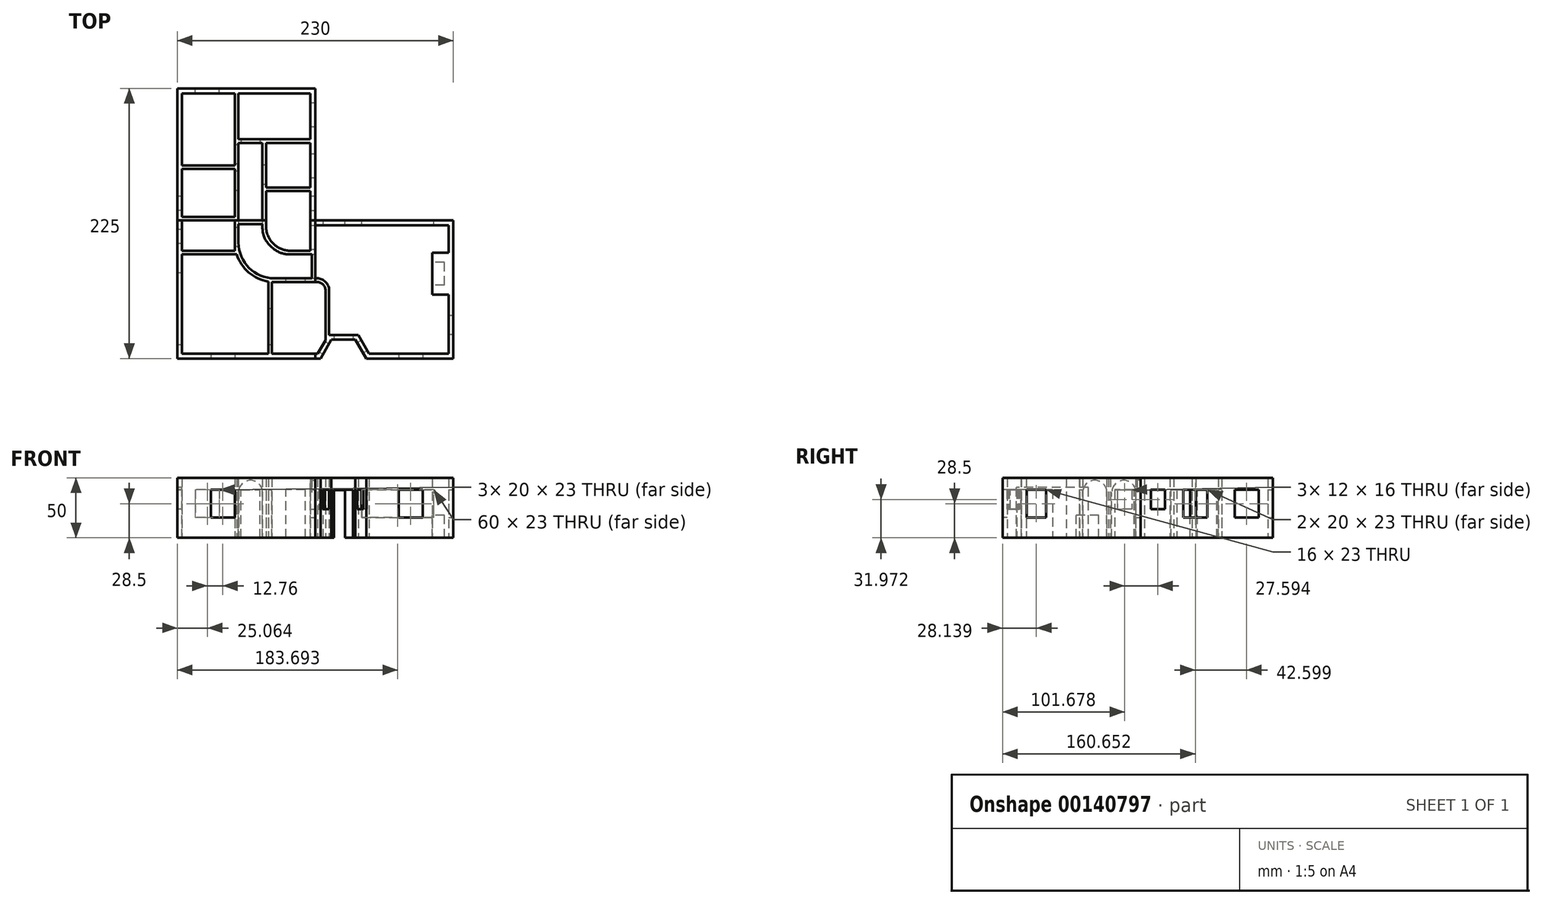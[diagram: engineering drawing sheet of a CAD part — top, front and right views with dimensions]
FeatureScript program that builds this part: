
annotation { "Feature Type Name" : "Feature", "Feature Type Description" : "" }
export const myFeature = defineFeature(function(context is Context, id is Id, definition is map)
    precondition{}
    {
        {
            var Q0;
            Q0=qCreatedBy(makeId("Top.planeOp"),FACE);
            var sketch = newSketch(context, id + "F0", { "sketchPlane" : qUnion([Q0])});
            skLineSegment(sketch, "E0", {"start": v(-116.87, 105.19) * mm, "end": v(-1.87, 105.19) * mm});
            skLineSegment(sketch, "E1", {"start": v(-116.87, 105.19) * mm, "end": v(-116.87, -4.81) * mm});
            skLineSegment(sketch, "E2", {"start": v(-1.87, 105.19) * mm, "end": v(-1.87, -4.81) * mm});
            skLineSegment(sketch, "E3", {"start": v(-116.87, -4.81) * mm, "end": v(-112.87, -4.81) * mm});
            skLineSegment(sketch, "E4", {"start": v(-112.87, 101.19) * mm, "end": v(-68.87, 101.19) * mm});
            skLineSegment(sketch, "E5", {"start": v(-5.87, 101.19) * mm, "end": v(-5.87, 62.93) * mm});
            skLineSegment(sketch, "E6", {"start": v(-5.87, -4.81) * mm, "end": v(-1.87, -4.81) * mm});
            skLineSegment(sketch, "E7", {"start": v(-112.87, -4.81) * mm, "end": v(-65.87, -4.81) * mm});
            skLineSegment(sketch, "E8", {"start": v(-5.87, 59.93) * mm, "end": v(-42.87, 59.93) * mm});
            skLineSegment(sketch, "E9", {"start": v(-45.87, 59.93) * mm, "end": v(-45.87, -4.81) * mm});
            skLineSegment(sketch, "E10", {"start": v(-45.87, -4.81) * mm, "end": v(-42.87, -4.81) * mm});
            skLineSegment(sketch, "E11", {"start": v(-68.87, 101.19) * mm, "end": v(-68.87, 41.19) * mm});
            skLineSegment(sketch, "E12", {"start": v(-112.87, 41.19) * mm, "end": v(-68.87, 41.19) * mm});
            skLineSegment(sketch, "E13", {"start": v(-112.87, -1.81) * mm, "end": v(-68.87, -1.81) * mm});
            skLineSegment(sketch, "E14", {"start": v(-65.87, 62.93) * mm, "end": v(-5.87, 62.93) * mm});
            skLineSegment(sketch, "E15", {"start": v(-42.87, 59.93) * mm, "end": v(-42.87, 22.68) * mm});
            skLineSegment(sketch, "E16", {"start": v(-5.87, 19.68) * mm, "end": v(-42.87, 19.68) * mm});
            skLineSegment(sketch, "E17", {"start": v(-42.87, 22.68) * mm, "end": v(-5.87, 22.68) * mm});
            skLineSegment(sketch, "E18.trimOffspring", {"start": v(-68.87, 38.19) * mm, "end": v(-68.87, -1.81) * mm});
            skLineSegment(sketch, "E19.trimOffspring", {"start": v(-65.87, 62.93) * mm, "end": v(-65.87, 101.19) * mm});
            skLineSegment(sketch, "E20.trimOffspring", {"start": v(-112.87, 41.19) * mm, "end": v(-112.87, 101.19) * mm});
            skLineSegment(sketch, "E21.trimOffspring", {"start": v(-42.87, 19.68) * mm, "end": v(-42.87, -4.81) * mm});
            skLineSegment(sketch, "E22.trimOffspring", {"start": v(-5.87, 19.68) * mm, "end": v(-5.87, -4.81) * mm});
            skLineSegment(sketch, "E23.trimOffspring", {"start": v(-5.87, 59.93) * mm, "end": v(-5.87, 22.68) * mm});
            skLineSegment(sketch, "E24.trimOffspring", {"start": v(-45.87, 59.93) * mm, "end": v(-65.87, 59.93) * mm});
            skLineSegment(sketch, "E25", {"start": v(-65.87, 59.93) * mm, "end": v(-65.87, -4.81) * mm});
            skLineSegment(sketch, "E26.trimOffspring", {"start": v(-65.87, 101.19) * mm, "end": v(-5.87, 101.19) * mm});
            skLineSegment(sketch, "E27", {"start": v(-112.87, -1.81) * mm, "end": v(-112.87, 38.19) * mm});
            skLineSegment(sketch, "E28", {"start": v(-112.87, 38.19) * mm, "end": v(-68.87, 38.19) * mm});
            skSolve(sketch);
        }
        {
            var Q0;
            Q0=makeQuery(id+"F0.imprint","IMPRINT",FACE,{"disambiguationData":[TD([[makeQuery(id+"F0.imprint","IMPRINT",EDGE,{"derivedFrom":sQuery(id+"F0.wireOp",EDGE,"E0")}),-1.0]])]});
            extrude(context, id + "F1", {"entities" : qUnion([Q0]), "depth" : 50 * mm});
        }
        {
            var Q0;
            Q0=makeQuery(id+"F1.opExtrude","SWEPT_FACE",FACE,{"disambiguationData":[OSD([sQuery(id+"F0.wireOp",EDGE,"E24.trimOffspring")])]});
            var sketch = newSketch(context, id + "F2", { "sketchPlane" : qUnion([Q0])});
            skLineSegment(sketch, "E29.bottom", {"start": v(-63.84, 0) * mm, "end": v(-47.84, 0) * mm});
            skLineSegment(sketch, "E29.top", {"start": v(-63.84, 40) * mm, "end": v(-47.84, 40) * mm});
            skLineSegment(sketch, "E29.left", {"start": v(-63.84, 0) * mm, "end": v(-63.84, 40) * mm});
            skLineSegment(sketch, "E29.right", {"start": v(-47.84, 0) * mm, "end": v(-47.84, 40) * mm});
            skSolve(sketch);
        }
        {
            var Q0;
            Q0=makeQuery(id+"F1.opExtrude","SWEPT_FACE",FACE,{"disambiguationData":[OSD([sQuery(id+"F0.wireOp",EDGE,"E25")])]});
            var sketch = newSketch(context, id + "F3", { "sketchPlane" : qUnion([Q0])});
            skLineSegment(sketch, "E30.bottom", {"start": v(58.58, 0) * mm, "end": v(42.58, 0) * mm});
            skLineSegment(sketch, "E30.top", {"start": v(58.58, 40) * mm, "end": v(42.58, 40) * mm});
            skLineSegment(sketch, "E30.left", {"start": v(58.58, 0) * mm, "end": v(58.58, 40) * mm});
            skLineSegment(sketch, "E30.right", {"start": v(42.58, 0) * mm, "end": v(42.58, 40) * mm});
            skLineSegment(sketch, "E31.bottom", {"start": v(20.48, 0) * mm, "end": v(36.48, 0) * mm});
            skLineSegment(sketch, "E31.top", {"start": v(20.48, 40) * mm, "end": v(36.48, 40) * mm});
            skLineSegment(sketch, "E31.left", {"start": v(20.48, 0) * mm, "end": v(20.48, 40) * mm});
            skLineSegment(sketch, "E31.right", {"start": v(36.48, 0) * mm, "end": v(36.48, 40) * mm});
            skSolve(sketch);
        }
        {
            var Q0;
            Q0=makeQuery(id+"F1.opExtrude","SWEPT_FACE",FACE,{"disambiguationData":[OSD([sQuery(id+"F0.wireOp",EDGE,"E9")])]});
            var sketch = newSketch(context, id + "F4", { "sketchPlane" : qUnion([Q0])});
            skLineSegment(sketch, "E32.bottom", {"start": v(-41.23, 0) * mm, "end": v(-25.23, 0) * mm});
            skLineSegment(sketch, "E32.top", {"start": v(-41.23, 40) * mm, "end": v(-25.23, 40) * mm});
            skLineSegment(sketch, "E32.left", {"start": v(-41.23, 0) * mm, "end": v(-41.23, 40) * mm});
            skLineSegment(sketch, "E32.right", {"start": v(-25.23, 0) * mm, "end": v(-25.23, 40) * mm});
            skSolve(sketch);
        }
        {
            var Q0;
            Q0=makeQuery(id+"F2.imprint","IMPRINT",FACE,{"disambiguationData":[TD([[makeQuery(id+"F2.imprint","IMPRINT",EDGE,{"derivedFrom":sQuery(id+"F2.wireOp",EDGE,"E29.bottom")}),-1.0]])]});
            extrude(context, id + "F5", {"entities" : qUnion([Q0]), "operationType" : NewBodyOperationType.REMOVE, "oppositeDirection" : true, "depth" : 10 * mm});
        }
        {
            var Q0;
            Q0=makeQuery(id+"F3.imprint","IMPRINT",FACE,{"disambiguationData":[TD([[makeQuery(id+"F3.imprint","IMPRINT",EDGE,{"derivedFrom":sQuery(id+"F3.wireOp",EDGE,"E30.bottom")}),-1.0]])]});
            var Q1;
            Q1=makeQuery(id+"F3.imprint","IMPRINT",FACE,{"disambiguationData":[TD([[makeQuery(id+"F3.imprint","IMPRINT",EDGE,{"derivedFrom":sQuery(id+"F3.wireOp",EDGE,"E31.bottom")}),-1.0]])]});
            extrude(context, id + "F6", {"entities" : qUnion([Q0, Q1]), "operationType" : NewBodyOperationType.REMOVE, "oppositeDirection" : true, "depth" : 10 * mm});
        }
        {
            var Q0;
            Q0=makeQuery(id+"F4.imprint","IMPRINT",FACE,{"disambiguationData":[TD([[makeQuery(id+"F4.imprint","IMPRINT",EDGE,{"derivedFrom":sQuery(id+"F4.wireOp",EDGE,"E32.bottom")}),1.0]])]});
            extrude(context, id + "F7", {"entities" : qUnion([Q0]), "operationType" : NewBodyOperationType.REMOVE, "oppositeDirection" : true, "depth" : 10 * mm});
        }
        {
            var Q0;
            Q0=makeQuery(id+"F1.opExtrude","SWEPT_FACE",FACE,{"disambiguationData":[OSD([sQuery(id+"F0.wireOp",EDGE,"E1")])]});
            var sketch = newSketch(context, id + "F8", { "sketchPlane" : qUnion([Q0])});
            skLineSegment(sketch, "E33.bottom", {"start": v(-15.46, 40) * mm, "end": v(-3.46, 40) * mm});
            skLineSegment(sketch, "E33.top", {"start": v(-15.46, 24) * mm, "end": v(-3.46, 24) * mm});
            skLineSegment(sketch, "E33.left", {"start": v(-15.46, 40) * mm, "end": v(-15.46, 24) * mm});
            skLineSegment(sketch, "E33.right", {"start": v(-3.46, 40) * mm, "end": v(-3.46, 24) * mm});
            skSolve(sketch);
        }
        {
            var Q0;
            Q0=makeQuery(id+"F1.opExtrude","SWEPT_FACE",FACE,{"disambiguationData":[OSD([sQuery(id+"F0.wireOp",EDGE,"E0")])]});
            var sketch = newSketch(context, id + "F9", { "sketchPlane" : qUnion([Q0])});
            skLineSegment(sketch, "E34.bottom", {"start": v(81.8, 40) * mm, "end": v(101.8, 40) * mm});
            skLineSegment(sketch, "E34.top", {"start": v(81.8, 17) * mm, "end": v(101.8, 17) * mm});
            skLineSegment(sketch, "E34.left", {"start": v(81.8, 40) * mm, "end": v(81.8, 17) * mm});
            skLineSegment(sketch, "E34.right", {"start": v(101.8, 40) * mm, "end": v(101.8, 17) * mm});
            skSolve(sketch);
        }
        {
            var Q0;
            Q0=makeQuery(id+"F1.opExtrude","SWEPT_FACE",FACE,{"disambiguationData":[OSD([sQuery(id+"F0.wireOp",EDGE,"E2")])]});
            var sketch = newSketch(context, id + "F10", { "sketchPlane" : qUnion([Q0])});
            skLineSegment(sketch, "E35.bottom", {"start": v(73.44, 40) * mm, "end": v(93.44, 40) * mm});
            skLineSegment(sketch, "E35.top", {"start": v(73.44, 17) * mm, "end": v(93.44, 17) * mm});
            skLineSegment(sketch, "E35.left", {"start": v(73.44, 40) * mm, "end": v(73.44, 17) * mm});
            skLineSegment(sketch, "E35.right", {"start": v(93.44, 40) * mm, "end": v(93.44, 17) * mm});
            skLineSegment(sketch, "E36.bottom", {"start": v(30.84, 40) * mm, "end": v(50.84, 40) * mm});
            skLineSegment(sketch, "E36.top", {"start": v(30.84, 17) * mm, "end": v(50.84, 17) * mm});
            skLineSegment(sketch, "E36.left", {"start": v(30.84, 40) * mm, "end": v(30.84, 17) * mm});
            skLineSegment(sketch, "E36.right", {"start": v(50.84, 40) * mm, "end": v(50.84, 17) * mm});
            skLineSegment(sketch, "E37.bottom", {"start": v(3.61, 40) * mm, "end": v(15.61, 40) * mm});
            skLineSegment(sketch, "E37.top", {"start": v(3.61, 24) * mm, "end": v(15.61, 24) * mm});
            skLineSegment(sketch, "E37.left", {"start": v(3.61, 40) * mm, "end": v(3.61, 24) * mm});
            skLineSegment(sketch, "E37.right", {"start": v(15.61, 40) * mm, "end": v(15.61, 24) * mm});
            skSolve(sketch);
        }
        {
            var Q0;
            Q0=makeQuery(id+"F8.imprint","IMPRINT",FACE,{"disambiguationData":[TD([[makeQuery(id+"F8.imprint","IMPRINT",EDGE,{"derivedFrom":sQuery(id+"F8.wireOp",EDGE,"E33.bottom")}),-1.0]])]});
            extrude(context, id + "F11", {"entities" : qUnion([Q0]), "operationType" : NewBodyOperationType.REMOVE, "oppositeDirection" : true, "depth" : 10 * mm});
        }
        {
            var Q0;
            Q0=makeQuery(id+"F9.imprint","IMPRINT",FACE,{"disambiguationData":[TD([[makeQuery(id+"F9.imprint","IMPRINT",EDGE,{"derivedFrom":sQuery(id+"F9.wireOp",EDGE,"E34.bottom")}),-1.0]])]});
            extrude(context, id + "F12", {"entities" : qUnion([Q0]), "operationType" : NewBodyOperationType.REMOVE, "oppositeDirection" : true, "depth" : 10 * mm});
        }
        {
            var Q0;
            Q0=makeQuery(id+"F10.imprint","IMPRINT",FACE,{"disambiguationData":[TD([[makeQuery(id+"F10.imprint","IMPRINT",EDGE,{"derivedFrom":sQuery(id+"F10.wireOp",EDGE,"E35.bottom")}),-1.0]])]});
            var Q1;
            Q1=makeQuery(id+"F10.imprint","IMPRINT",FACE,{"disambiguationData":[TD([[makeQuery(id+"F10.imprint","IMPRINT",EDGE,{"derivedFrom":sQuery(id+"F10.wireOp",EDGE,"E36.bottom")}),-1.0]])]});
            var Q2;
            Q2=makeQuery(id+"F10.imprint","IMPRINT",FACE,{"disambiguationData":[TD([[makeQuery(id+"F10.imprint","IMPRINT",EDGE,{"derivedFrom":sQuery(id+"F10.wireOp",EDGE,"E37.bottom")}),-1.0]])]});
            extrude(context, id + "F13", {"entities" : qUnion([Q0, Q1, Q2]), "operationType" : NewBodyOperationType.REMOVE, "oppositeDirection" : true, "depth" : 10 * mm});
        }
        {
            var Q0;
            Q0=makeQuery(id+"F0.imprint","IMPRINT",FACE,{"disambiguationData":[TD([[makeQuery(id+"F0.imprint","IMPRINT",EDGE,{"derivedFrom":sQuery(id+"F0.wireOp",EDGE,"E0")}),-1.0]])]});
            var sketch = newSketch(context, id + "F14", { "sketchPlane" : qUnion([Q0])});
            skLineSegment(sketch, "E38", {"start": v(-116.87, -4.81) * mm, "end": v(-116.87, -119.81) * mm});
            skLineSegment(sketch, "E39", {"start": v(-116.87, -119.81) * mm, "end": v(-1.87, -119.81) * mm});
            skLineSegment(sketch, "E40", {"start": v(-1.87, -119.81) * mm, "end": v(-1.87, -115.81) * mm});
            skLineSegment(sketch, "E41", {"start": v(-4.87, -115.81) * mm, "end": v(-38.04, -115.81) * mm});
            skLineSegment(sketch, "E42", {"start": v(-112.87, -115.81) * mm, "end": v(-112.87, -33.06) * mm});
            skLineSegment(sketch, "E43", {"start": v(-112.87, -4.81) * mm, "end": v(-116.87, -4.81) * mm});
            skLineSegment(sketch, "E44", {"start": v(-65.87, -7.81) * mm, "end": v(-65.87, -23.04) * mm});
            skPoint(sketch, "E44.startSnap0", {"position": v(-114.87, -4.81) * mm});
            skLineSegment(sketch, "E45", {"start": v(-38.04, -56.04) * mm, "end": v(-38.04, -115.81) * mm});
            skLineSegment(sketch, "E46", {"start": v(-35.87, -53.04) * mm, "end": v(-4.87, -53.04) * mm});
            skLineSegment(sketch, "E47", {"start": v(-1.87, -53.04) * mm, "end": v(-1.87, -56.04) * mm});
            skLineSegment(sketch, "E48", {"start": v(-68.87, -30.06) * mm, "end": v(-112.87, -30.06) * mm});
            skLineSegment(sketch, "E49", {"start": v(-45.87, -7.81) * mm, "end": v(-45.87, -11.21) * mm});
            skLineSegment(sketch, "E50", {"start": v(-38.6, -26.64) * mm, "end": v(-36.4, -28.46) * mm});
            skLineSegment(sketch, "E51", {"start": v(-23.66, -33.04) * mm, "end": v(-4.87, -33.04) * mm});
            skLineSegment(sketch, "E52", {"start": v(-1.87, -33.04) * mm, "end": v(-1.87, -4.81) * mm});
            skLineSegment(sketch, "E53", {"start": v(-1.87, -4.81) * mm, "end": v(-5.87, -4.81) * mm});
            skLineSegment(sketch, "E54", {"start": v(-5.87, -4.81) * mm, "end": v(-5.87, -30.04) * mm});
            skLineSegment(sketch, "E55", {"start": v(-5.87, -30.04) * mm, "end": v(-22.58, -30.04) * mm});
            skLineSegment(sketch, "E56", {"start": v(-35.32, -25.46) * mm, "end": v(-35.6, -25.22) * mm});
            skLineSegment(sketch, "E57", {"start": v(-42.87, -9.8) * mm, "end": v(-42.87, -4.81) * mm});
            skLineSegment(sketch, "E58", {"start": v(-42.87, -4.81) * mm, "end": v(-45.87, -4.81) * mm});
            skLineSegment(sketch, "E59", {"start": v(-112.87, -33.06) * mm, "end": v(-67.31, -33.06) * mm});
            skLineSegment(sketch, "E60", {"start": v(-41.04, -115.81) * mm, "end": v(-41.04, -55.63) * mm});
            skLineSegment(sketch, "E61", {"start": v(-68.87, -30.06) * mm, "end": v(-68.87, -4.81) * mm});
            skLineSegment(sketch, "E62", {"start": v(-4.87, -56.04) * mm, "end": v(-38.04, -56.04) * mm});
            skLineSegment(sketch, "E63.trimOffspring", {"start": v(-112.87, -30.06) * mm, "end": v(-112.87, -4.81) * mm});
            skLineSegment(sketch, "E64", {"start": v(-1.87, -53.04) * mm, "end": v(-1.87, -33.04) * mm});
            skLineSegment(sketch, "E65", {"start": v(-4.87, -53.04) * mm, "end": v(-4.87, -33.04) * mm});
            skLineSegment(sketch, "E66", {"start": v(-65.87, -4.81) * mm, "end": v(-45.87, -4.81) * mm});
            skLineSegment(sketch, "E67", {"start": v(-65.87, -7.81) * mm, "end": v(-45.87, -7.81) * mm});
            skLineSegment(sketch, "E68", {"start": v(-65.87, -4.81) * mm, "end": v(-68.87, -4.81) * mm});
            skLineSegment(sketch, "E69.trimOffspring", {"start": v(-41.04, -115.81) * mm, "end": v(-112.87, -115.81) * mm});
            skPoint(sketch, "E70.visualSharp", {"position": v(-42.87, -19.22) * mm});
            skArc(sketch, "E70.filletArc", {"start": v(-42.87, -9.8) * mm, "mid": v(-40.96, -18.32) * mm, "end": v(-35.6, -25.22) * mm});
            skPoint(sketch, "E71.visualSharp", {"position": v(-29.77, -30.04) * mm});
            skArc(sketch, "E71.filletArc", {"start": v(-35.32, -25.46) * mm, "mid": v(-29.35, -28.86) * mm, "end": v(-22.58, -30.04) * mm});
            skPoint(sketch, "E72.visualSharp", {"position": v(-45.87, -20.64) * mm});
            skArc(sketch, "E72.filletArc", {"start": v(-45.87, -11.21) * mm, "mid": v(-43.96, -19.74) * mm, "end": v(-38.6, -26.64) * mm});
            skPoint(sketch, "E73.visualSharp", {"position": v(-30.85, -33.04) * mm});
            skArc(sketch, "E73.filletArc", {"start": v(-36.4, -28.46) * mm, "mid": v(-30.43, -31.86) * mm, "end": v(-23.66, -33.04) * mm});
            skPoint(sketch, "E74.visualSharp", {"position": v(-65.87, -53.04) * mm});
            skArc(sketch, "E74.filletArc", {"start": v(-65.87, -23.04) * mm, "mid": v(-57.09, -44.25) * mm, "end": v(-35.87, -53.04) * mm});
            skArc(sketch, "E75.0", {"start": v(-67.31, -33.06) * mm, "mid": v(-57.37, -48.07) * mm, "end": v(-41.04, -55.63) * mm});
            skLineSegment(sketch, "E76", {"start": v(-4.87, -56.04) * mm, "end": v(-1.87, -56.04) * mm});
            skLineSegment(sketch, "E77", {"start": v(-1.87, -115.81) * mm, "end": v(-4.87, -115.81) * mm});
            skSolve(sketch);
        }
        {
            var Q0;
            Q0=makeQuery(id+"F14.imprint","IMPRINT",FACE,{"disambiguationData":[TD([[makeQuery(id+"F14.imprint","IMPRINT",EDGE,{"derivedFrom":sQuery(id+"F14.wireOp",EDGE,"E38")}),1.0]])]});
            extrude(context, id + "F15", {"entities" : qUnion([Q0]), "depth" : 50 * mm});
        }
        {
            var Q0;
            Q0=makeQuery(id+"F15.opExtrude","SWEPT_FACE",FACE,{"disambiguationData":[OSD([sQuery(id+"F14.wireOp",EDGE,"E40"),sQuery(id+"F14.wireOp",EDGE,"E47"),sQuery(id+"F14.wireOp",EDGE,"E52"),sQuery(id+"F14.wireOp",EDGE,"E64")])]});
            var sketch = newSketch(context, id + "F16", { "sketchPlane" : qUnion([Q0])});
            skLineSegment(sketch, "E78.bottom", {"start": v(-53.04, 0) * mm, "end": v(-33.04, 0) * mm});
            skLineSegment(sketch, "E78.left", {"start": v(-53.04, 0) * mm, "end": v(-53.04, 38) * mm});
            skLineSegment(sketch, "E78.right", {"start": v(-33.04, 0) * mm, "end": v(-33.04, 38) * mm});
            skArc(sketch, "E79", {"start": v(-33.04, 38) * mm, "mid": v(-43.04, 48) * mm, "end": v(-53.04, 38) * mm});
            skLineSegment(sketch, "E80.bottom", {"start": v(-28.81, 0) * mm, "end": v(-8.81, 0) * mm});
            skLineSegment(sketch, "E80.left", {"start": v(-28.81, 0) * mm, "end": v(-28.81, 38) * mm});
            skLineSegment(sketch, "E80.right", {"start": v(-8.81, 0) * mm, "end": v(-8.81, 38) * mm});
            skArc(sketch, "E81", {"start": v(-8.81, 38) * mm, "mid": v(-18.81, 48) * mm, "end": v(-28.81, 38) * mm});
            skSolve(sketch);
        }
        {
            var Q0;
            Q0=makeQuery(id+"F16.imprint","IMPRINT",FACE,{"disambiguationData":[TD([[makeQuery(id+"F16.imprint","IMPRINT",EDGE,{"derivedFrom":sQuery(id+"F16.wireOp",EDGE,"E78.bottom")}),-1.0]])]});
            var Q1;
            Q1=makeQuery(id+"F16.imprint","IMPRINT",FACE,{"disambiguationData":[TD([[makeQuery(id+"F16.imprint","IMPRINT",EDGE,{"derivedFrom":sQuery(id+"F16.wireOp",EDGE,"E80.bottom")}),-1.0]])]});
            extrude(context, id + "F17", {"entities" : qUnion([Q0, Q1]), "operationType" : NewBodyOperationType.REMOVE, "oppositeDirection" : true, "depth" : 10 * mm});
        }
        {
            var Q0;
            Q0=makeQuery(id+"F15.opExtrude","SWEPT_FACE",FACE,{"disambiguationData":[OSD([sQuery(id+"F14.wireOp",EDGE,"E44")])]});
            var sketch = newSketch(context, id + "F18", { "sketchPlane" : qUnion([Q0])});
            skLineSegment(sketch, "E82.bottom", {"start": v(-10.38, 0) * mm, "end": v(-26.38, 0) * mm});
            skLineSegment(sketch, "E82.top", {"start": v(-10.38, 40) * mm, "end": v(-26.38, 40) * mm});
            skLineSegment(sketch, "E82.left", {"start": v(-10.38, 0) * mm, "end": v(-10.38, 40) * mm});
            skLineSegment(sketch, "E82.right", {"start": v(-26.38, 0) * mm, "end": v(-26.38, 40) * mm});
            skSolve(sketch);
        }
        {
            var Q0;
            {var subQ4=sQuery(id+"F18.wireOp",EDGE,"E82.left");Q0=makeQuery(id+"F18.imprint","IMPRINT",FACE,{"disambiguationData":[TD([[makeQuery(id+"F18.imprint","IMPRINT",EDGE,{"derivedFrom":subQ4}),1.0]])]});}
            var Q1;
            {var subQ3=sQuery(id+"F18.wireOp",EDGE,"E82.right");Q1=makeQuery(id+"F18.imprint","IMPRINT",FACE,{"disambiguationData":[TD([[makeQuery(id+"F18.imprint","IMPRINT",EDGE,{"derivedFrom":subQ3}),-1.0]])]});}
            extrude(context, id + "F19", {"entities" : qUnion([Q0, Q1]), "operationType" : NewBodyOperationType.REMOVE, "endBound" : BoundingType.SYMMETRIC, "oppositeDirection" : true, "depth" : 10 * mm});
        }
        {
            var Q0;
            Q0=makeQuery(id+"F15.opExtrude","SWEPT_FACE",FACE,{"disambiguationData":[OSD([sQuery(id+"F14.wireOp",EDGE,"E67")])]});
            var sketch = newSketch(context, id + "F20", { "sketchPlane" : qUnion([Q0])});
            skLineSegment(sketch, "E83.bottom", {"start": v(-65.87, 0) * mm, "end": v(-45.87, 0) * mm});
            skLineSegment(sketch, "E83.left", {"start": v(-65.87, 0) * mm, "end": v(-65.87, 38) * mm});
            skLineSegment(sketch, "E83.right", {"start": v(-45.87, 0) * mm, "end": v(-45.87, 38) * mm});
            skArc(sketch, "E84", {"start": v(-45.87, 38) * mm, "mid": v(-55.87, 48) * mm, "end": v(-65.87, 38) * mm});
            skSolve(sketch);
        }
        {
            var Q0;
            Q0=makeQuery(id+"F20.imprint","IMPRINT",FACE,{"disambiguationData":[TD([[makeQuery(id+"F20.imprint","IMPRINT",EDGE,{"derivedFrom":sQuery(id+"F20.wireOp",EDGE,"E83.bottom")}),1.0]])]});
            extrude(context, id + "F21", {"entities" : qUnion([Q0]), "operationType" : NewBodyOperationType.REMOVE, "oppositeDirection" : true, "depth" : 10 * mm});
        }
        {
            var Q0;
            Q0=makeQuery(id+"F17.boolean.opBoolean","MERGE",FACE,{"derivedFrom":[makeQuery(id+"F15.opExtrude","SWEPT_FACE",FACE,{"disambiguationData":[OSD([sQuery(id+"F14.wireOp",EDGE,"E46")])]}),makeQuery(id+"F17.opExtrude","SWEPT_FACE",FACE,{"disambiguationData":[OSD([sQuery(id+"F16.wireOp",EDGE,"E78.left")])]})]});
            var sketch = newSketch(context, id + "F22", { "sketchPlane" : qUnion([Q0])});
            skLineSegment(sketch, "E85.bottom", {"start": v(10.23, 0) * mm, "end": v(26.23, 0) * mm});
            skLineSegment(sketch, "E85.top", {"start": v(10.23, 40) * mm, "end": v(26.23, 40) * mm});
            skLineSegment(sketch, "E85.left", {"start": v(10.23, 0) * mm, "end": v(10.23, 40) * mm});
            skLineSegment(sketch, "E85.right", {"start": v(26.23, 0) * mm, "end": v(26.23, 40) * mm});
            skSolve(sketch);
        }
        {
            var Q0;
            Q0=makeQuery(id+"F22.imprint","IMPRINT",FACE,{"disambiguationData":[TD([[makeQuery(id+"F22.imprint","IMPRINT",EDGE,{"derivedFrom":sQuery(id+"F22.wireOp",EDGE,"E85.bottom")}),-1.0]])]});
            extrude(context, id + "F23", {"entities" : qUnion([Q0]), "operationType" : NewBodyOperationType.REMOVE, "oppositeDirection" : true, "depth" : 10 * mm});
        }
        {
            var Q0;
            Q0=makeQuery(id+"F15.opExtrude","SWEPT_FACE",FACE,{"disambiguationData":[OSD([sQuery(id+"F14.wireOp",EDGE,"E45")])]});
            var sketch = newSketch(context, id + "F24", { "sketchPlane" : qUnion([Q0])});
            skLineSegment(sketch, "E86.bottom", {"start": v(-108.14, 0) * mm, "end": v(-78.14, 0) * mm});
            skLineSegment(sketch, "E86.top", {"start": v(-108.14, 40) * mm, "end": v(-78.14, 40) * mm});
            skLineSegment(sketch, "E86.left", {"start": v(-108.14, 0) * mm, "end": v(-108.14, 40) * mm});
            skLineSegment(sketch, "E86.right", {"start": v(-78.14, 0) * mm, "end": v(-78.14, 40) * mm});
            skSolve(sketch);
        }
        {
            var Q0;
            Q0=makeQuery(id+"F24.imprint","IMPRINT",FACE,{"disambiguationData":[TD([[makeQuery(id+"F24.imprint","IMPRINT",EDGE,{"derivedFrom":sQuery(id+"F24.wireOp",EDGE,"E86.bottom")}),-1.0]])]});
            extrude(context, id + "F25", {"entities" : qUnion([Q0]), "operationType" : NewBodyOperationType.REMOVE, "oppositeDirection" : true, "depth" : 10 * mm});
        }
        {
            var Q0;
            Q0=makeQuery(id+"F15.opExtrude","SWEPT_FACE",FACE,{"disambiguationData":[OSD([sQuery(id+"F14.wireOp",EDGE,"E38")])]});
            var sketch = newSketch(context, id + "F26", { "sketchPlane" : qUnion([Q0])});
            skLineSegment(sketch, "E87.bottom", {"start": v(12.13, 39.97) * mm, "end": v(24.13, 39.97) * mm});
            skLineSegment(sketch, "E87.top", {"start": v(12.13, 23.97) * mm, "end": v(24.13, 23.97) * mm});
            skLineSegment(sketch, "E87.left", {"start": v(12.13, 39.97) * mm, "end": v(12.13, 23.97) * mm});
            skLineSegment(sketch, "E87.right", {"start": v(24.13, 39.97) * mm, "end": v(24.13, 23.97) * mm});
            skLineSegment(sketch, "E88.bottom", {"start": v(48.39, 0) * mm, "end": v(108.39, 0) * mm});
            skLineSegment(sketch, "E88.top", {"start": v(48.39, 42) * mm, "end": v(108.39, 42) * mm});
            skLineSegment(sketch, "E88.left", {"start": v(48.39, 0) * mm, "end": v(48.39, 42) * mm});
            skLineSegment(sketch, "E88.right", {"start": v(108.39, 0) * mm, "end": v(108.39, 42) * mm});
            skSolve(sketch);
        }
        {
            var Q0;
            Q0=makeQuery(id+"F26.imprint","IMPRINT",FACE,{"disambiguationData":[TD([[makeQuery(id+"F26.imprint","IMPRINT",EDGE,{"derivedFrom":sQuery(id+"F26.wireOp",EDGE,"E88.bottom")}),1.0]])]});
            var Q1;
            Q1=makeQuery(id+"F26.imprint","IMPRINT",FACE,{"disambiguationData":[TD([[makeQuery(id+"F26.imprint","IMPRINT",EDGE,{"derivedFrom":sQuery(id+"F26.wireOp",EDGE,"E87.bottom")}),-1.0]])]});
            extrude(context, id + "F27", {"entities" : qUnion([Q0, Q1]), "operationType" : NewBodyOperationType.REMOVE, "oppositeDirection" : true, "depth" : 10 * mm});
        }
        {
            var Q0;
            Q0=qCreatedBy(makeId("Top.planeOp"),FACE);
            var sketch = newSketch(context, id + "F28", { "sketchPlane" : qUnion([Q0])});
            skLineSegment(sketch, "E89", {"start": v(-1.87, -4.81) * mm, "end": v(113.13, -4.81) * mm});
            skLineSegment(sketch, "E90", {"start": v(113.13, -4.81) * mm, "end": v(113.13, -119.81) * mm});
            skLineSegment(sketch, "E91", {"start": v(113.13, -119.81) * mm, "end": v(40.63, -119.81) * mm});
            skLineSegment(sketch, "E92", {"start": v(109.13, -8.81) * mm, "end": v(109.13, -31.61) * mm});
            skLineSegment(sketch, "E93", {"start": v(109.13, -115.81) * mm, "end": v(42.94, -115.81) * mm});
            skLineSegment(sketch, "E94", {"start": v(109.13, -8.81) * mm, "end": v(-1.87, -8.81) * mm});
            skLineSegment(sketch, "E95", {"start": v(-1.87, -119.81) * mm, "end": v(-1.87, -115.81) * mm});
            skLineSegment(sketch, "E96", {"start": v(-1.87, -8.81) * mm, "end": v(-1.87, -4.81) * mm});
            skLineSegment(sketch, "E97", {"start": v(6.6, -104.63) * mm, "end": v(6.6, -63.04) * mm});
            skLineSegment(sketch, "E98", {"start": v(9.6, -100.08) * mm, "end": v(33.85, -100.08) * mm});
            skLineSegment(sketch, "E99", {"start": v(33.85, -100.08) * mm, "end": v(42.94, -115.81) * mm});
            skLineSegment(sketch, "E100", {"start": v(11.54, -104.08) * mm, "end": v(31.54, -104.08) * mm});
            skLineSegment(sketch, "E101", {"start": v(31.54, -104.08) * mm, "end": v(40.63, -119.81) * mm});
            skLineSegment(sketch, "E102.trimOffspring", {"start": v(2.46, -119.81) * mm, "end": v(-1.87, -119.81) * mm});
            skLineSegment(sketch, "E103", {"start": v(109.13, -66.61) * mm, "end": v(95.6, -66.61) * mm});
            skLineSegment(sketch, "E104", {"start": v(95.6, -66.61) * mm, "end": v(95.6, -31.61) * mm});
            skLineSegment(sketch, "E105", {"start": v(95.6, -31.61) * mm, "end": v(109.13, -31.61) * mm});
            skLineSegment(sketch, "E106.trimOffspring", {"start": v(109.13, -66.61) * mm, "end": v(109.13, -115.81) * mm});
            skLineSegment(sketch, "E107", {"start": v(-0.4, -53.04) * mm, "end": v(-1.87, -53.04) * mm});
            skLineSegment(sketch, "E108", {"start": v(9.6, -63.04) * mm, "end": v(9.6, -100.08) * mm});
            skPoint(sketch, "E109.visualSharp", {"position": v(9.6, -53.04) * mm});
            skArc(sketch, "E109.filletArc", {"start": v(9.6, -63.04) * mm, "mid": v(6.67, -55.97) * mm, "end": v(-0.4, -53.04) * mm});
            skLineSegment(sketch, "E110.0", {"start": v(-0.4, -56.04) * mm, "end": v(-1.87, -56.04) * mm});
            skArc(sketch, "E110.1", {"start": v(6.6, -63.04) * mm, "mid": v(4.55, -58.1) * mm, "end": v(-0.4, -56.04) * mm});
            skLineSegment(sketch, "E111", {"start": v(-1.87, -56.04) * mm, "end": v(-1.87, -53.04) * mm});
            skLineSegment(sketch, "E112", {"start": v(11.54, -104.08) * mm, "end": v(2.46, -119.81) * mm});
            skLineSegment(sketch, "E113.0", {"start": v(6.6, -104.63) * mm, "end": v(0.15, -115.81) * mm});
            skLineSegment(sketch, "E114.trimOffspring", {"start": v(0.15, -115.81) * mm, "end": v(-1.87, -115.81) * mm});
            skSolve(sketch);
        }
        {
            var Q0;
            Q0=makeQuery(id+"F28.imprint","IMPRINT",FACE,{"disambiguationData":[TD([[makeQuery(id+"F28.imprint","IMPRINT",EDGE,{"derivedFrom":sQuery(id+"F28.wireOp",EDGE,"E89")}),-1.0]])]});
            extrude(context, id + "F29", {"entities" : qUnion([Q0]), "depth" : 50 * mm});
        }
        {
            var Q0;
            Q0=makeQuery(id+"F15.opExtrude","SWEPT_FACE",FACE,{"disambiguationData":[OSD([sQuery(id+"F14.wireOp",EDGE,"E39")])]});
            var sketch = newSketch(context, id + "F30", { "sketchPlane" : qUnion([Q0])});
            skLineSegment(sketch, "E115.bottom", {"start": v(-89.05, 40) * mm, "end": v(-69.05, 40) * mm});
            skLineSegment(sketch, "E115.top", {"start": v(-89.05, 17) * mm, "end": v(-69.05, 17) * mm});
            skLineSegment(sketch, "E115.left", {"start": v(-89.05, 40) * mm, "end": v(-89.05, 17) * mm});
            skLineSegment(sketch, "E115.right", {"start": v(-69.05, 40) * mm, "end": v(-69.05, 17) * mm});
            skSolve(sketch);
        }
        {
            var Q0;
            Q0=makeQuery(id+"F30.imprint","IMPRINT",FACE,{"disambiguationData":[TD([[makeQuery(id+"F30.imprint","IMPRINT",EDGE,{"derivedFrom":sQuery(id+"F30.wireOp",EDGE,"E115.bottom")}),-1.0]])]});
            extrude(context, id + "F31", {"entities" : qUnion([Q0]), "operationType" : NewBodyOperationType.REMOVE, "oppositeDirection" : true, "depth" : 10 * mm});
        }
        {
            var Q0;
            Q0=makeQuery(id+"F29.opExtrude","SWEPT_FACE",FACE,{"disambiguationData":[OSD([sQuery(id+"F28.wireOp",EDGE,"E112")])]});
            var sketch = newSketch(context, id + "F32", { "sketchPlane" : qUnion([Q0])});
            skLineSegment(sketch, "E116.bottom", {"start": v(-98.43, 40) * mm, "end": v(-88.43, 40) * mm});
            skLineSegment(sketch, "E116.top", {"start": v(-98.43, 24) * mm, "end": v(-88.43, 24) * mm});
            skLineSegment(sketch, "E116.left", {"start": v(-98.43, 40) * mm, "end": v(-98.43, 24) * mm});
            skLineSegment(sketch, "E116.right", {"start": v(-88.43, 40) * mm, "end": v(-88.43, 24) * mm});
            skSolve(sketch);
        }
        {
            var Q0;
            Q0=makeQuery(id+"F32.imprint","IMPRINT",FACE,{"disambiguationData":[TD([[makeQuery(id+"F32.imprint","IMPRINT",EDGE,{"derivedFrom":sQuery(id+"F32.wireOp",EDGE,"E116.bottom")}),-1.0]])]});
            extrude(context, id + "F33", {"entities" : qUnion([Q0]), "operationType" : NewBodyOperationType.REMOVE, "oppositeDirection" : true, "depth" : 10 * mm});
        }
        {
            var Q0;
            Q0=makeQuery(id+"F29.opExtrude","SWEPT_FACE",FACE,{"disambiguationData":[OSD([sQuery(id+"F28.wireOp",EDGE,"E101")])]});
            var sketch = newSketch(context, id + "F34", { "sketchPlane" : qUnion([Q0])});
            skLineSegment(sketch, "E117.bottom", {"start": v(108.83, 40) * mm, "end": v(118.83, 40) * mm});
            skLineSegment(sketch, "E117.top", {"start": v(108.83, 24) * mm, "end": v(118.83, 24) * mm});
            skLineSegment(sketch, "E117.left", {"start": v(108.83, 40) * mm, "end": v(108.83, 24) * mm});
            skLineSegment(sketch, "E117.right", {"start": v(118.83, 40) * mm, "end": v(118.83, 24) * mm});
            skSolve(sketch);
        }
        {
            var Q0;
            Q0=makeQuery(id+"F34.imprint","IMPRINT",FACE,{"disambiguationData":[TD([[makeQuery(id+"F34.imprint","IMPRINT",EDGE,{"derivedFrom":sQuery(id+"F34.wireOp",EDGE,"E117.bottom")}),-1.0]])]});
            extrude(context, id + "F35", {"entities" : qUnion([Q0]), "operationType" : NewBodyOperationType.REMOVE, "oppositeDirection" : true, "depth" : 10 * mm});
        }
        {
            var Q0;
            Q0=makeQuery(id+"F29.opExtrude","SWEPT_FACE",FACE,{"disambiguationData":[OSD([sQuery(id+"F28.wireOp",EDGE,"E100")])]});
            var sketch = newSketch(context, id + "F36", { "sketchPlane" : qUnion([Q0])});
            skLineSegment(sketch, "E118.bottom", {"start": v(13.57, 0) * mm, "end": v(29.57, 0) * mm});
            skLineSegment(sketch, "E118.top", {"start": v(13.57, 40) * mm, "end": v(29.57, 40) * mm});
            skLineSegment(sketch, "E118.left", {"start": v(13.57, 0) * mm, "end": v(13.57, 40) * mm});
            skLineSegment(sketch, "E118.right", {"start": v(29.57, 0) * mm, "end": v(29.57, 40) * mm});
            skSolve(sketch);
        }
        {
            var Q0;
            Q0=makeQuery(id+"F36.imprint","IMPRINT",FACE,{"disambiguationData":[TD([[makeQuery(id+"F36.imprint","IMPRINT",EDGE,{"derivedFrom":sQuery(id+"F36.wireOp",EDGE,"E118.bottom")}),1.0]])]});
            extrude(context, id + "F37", {"entities" : qUnion([Q0]), "operationType" : NewBodyOperationType.REMOVE, "oppositeDirection" : true, "depth" : 10 * mm});
        }
        {
            var Q0;
            Q0=makeQuery(id+"F29.opExtrude","SWEPT_FACE",FACE,{"disambiguationData":[OSD([sQuery(id+"F28.wireOp",EDGE,"E91")])]});
            var sketch = newSketch(context, id + "F38", { "sketchPlane" : qUnion([Q0])});
            skLineSegment(sketch, "E119.bottom", {"start": v(67.53, 40) * mm, "end": v(87.53, 40) * mm});
            skLineSegment(sketch, "E119.top", {"start": v(67.53, 17) * mm, "end": v(87.53, 17) * mm});
            skLineSegment(sketch, "E119.left", {"start": v(67.53, 40) * mm, "end": v(67.53, 17) * mm});
            skLineSegment(sketch, "E119.right", {"start": v(87.53, 40) * mm, "end": v(87.53, 17) * mm});
            skSolve(sketch);
        }
        {
            var Q0;
            Q0 = qSketchRegion(id + "F38", true);
            extrude(context, id + "F39", {"entities" : qUnion([Q0]), "operationType" : NewBodyOperationType.REMOVE, "oppositeDirection" : true, "depth" : 10 * mm});
        }
        {
            var Q0;
            Q0=makeQuery(id+"F29.opExtrude","SWEPT_FACE",FACE,{"disambiguationData":[OSD([sQuery(id+"F28.wireOp",EDGE,"E89")])]});
            var sketch = newSketch(context, id + "F40", { "sketchPlane" : qUnion([Q0])});
            skLineSegment(sketch, "E120.top", {"start": v(-96.82, 40) * mm, "end": v(-36.82, 40) * mm});
            skLineSegment(sketch, "E120.left", {"start": v(-96.82, 17) * mm, "end": v(-96.82, 40) * mm});
            skLineSegment(sketch, "E120.right", {"start": v(-36.82, 17) * mm, "end": v(-36.82, 40) * mm});
            skLineSegment(sketch, "E121", {"start": v(-96.82, 17) * mm, "end": v(-36.82, 17) * mm});
            skLineSegment(sketch, "E122.bottom", {"start": v(-4.87, 0) * mm, "end": v(-22.87, 0) * mm});
            skLineSegment(sketch, "E122.top", {"start": v(-4.87, 39.91) * mm, "end": v(-22.87, 39.91) * mm});
            skLineSegment(sketch, "E122.left", {"start": v(-4.87, 0) * mm, "end": v(-4.87, 39.91) * mm});
            skLineSegment(sketch, "E122.right", {"start": v(-22.87, 0) * mm, "end": v(-22.87, 39.91) * mm});
            skSolve(sketch);
        }
        {
            var Q0;
            Q0 = qSketchRegion(id + "F40", true);
            extrude(context, id + "F41", {"entities" : qUnion([Q0]), "operationType" : NewBodyOperationType.REMOVE, "oppositeDirection" : true, "depth" : 10 * mm});
        }
        {
            var Q0;
            Q0=makeQuery(id+"F29.opExtrude","SWEPT_FACE",FACE,{"disambiguationData":[OSD([sQuery(id+"F28.wireOp",EDGE,"E104")])]});
            var sketch = newSketch(context, id + "F42", { "sketchPlane" : qUnion([Q0])});
            skLineSegment(sketch, "E123.bottom", {"start": v(39.61, 0) * mm, "end": v(58.61, 0) * mm});
            skLineSegment(sketch, "E123.top", {"start": v(39.61, 18.96) * mm, "end": v(58.61, 18.96) * mm});
            skLineSegment(sketch, "E123.left", {"start": v(39.61, 0) * mm, "end": v(39.61, 18.96) * mm});
            skLineSegment(sketch, "E123.right", {"start": v(58.61, 0) * mm, "end": v(58.61, 18.96) * mm});
            skSolve(sketch);
        }
        {
            var Q0;
            Q0=makeQuery(id+"F42.imprint","IMPRINT",FACE,{"disambiguationData":[TD([[makeQuery(id+"F42.imprint","IMPRINT",EDGE,{"derivedFrom":sQuery(id+"F42.wireOp",EDGE,"E123.bottom")}),-1.0]])]});
            extrude(context, id + "F43", {"entities" : qUnion([Q0]), "operationType" : NewBodyOperationType.REMOVE, "oppositeDirection" : true, "depth" : 10 * mm});
        }
        {
            var Q0;
            Q0=makeQuery(id+"F29.opExtrude","SWEPT_FACE",FACE,{"disambiguationData":[OSD([sQuery(id+"F28.wireOp",EDGE,"E90")])]});
            var sketch = newSketch(context, id + "F44", { "sketchPlane" : qUnion([Q0])});
            skLineSegment(sketch, "E124.bottom", {"start": v(-99.67, 40) * mm, "end": v(-83.67, 40) * mm});
            skLineSegment(sketch, "E124.top", {"start": v(-99.67, 17) * mm, "end": v(-83.67, 17) * mm});
            skLineSegment(sketch, "E124.left", {"start": v(-99.67, 40) * mm, "end": v(-99.67, 17) * mm});
            skLineSegment(sketch, "E124.right", {"start": v(-83.67, 40) * mm, "end": v(-83.67, 17) * mm});
            skSolve(sketch);
        }
        {
            var Q0;
            Q0=makeQuery(id+"F44.imprint","IMPRINT",FACE,{"disambiguationData":[TD([[makeQuery(id+"F44.imprint","IMPRINT",EDGE,{"derivedFrom":sQuery(id+"F44.wireOp",EDGE,"E124.bottom")}),-1.0]])]});
            extrude(context, id + "F45", {"entities" : qUnion([Q0]), "operationType" : NewBodyOperationType.REMOVE, "oppositeDirection" : true, "depth" : 10 * mm});
        }
    });
